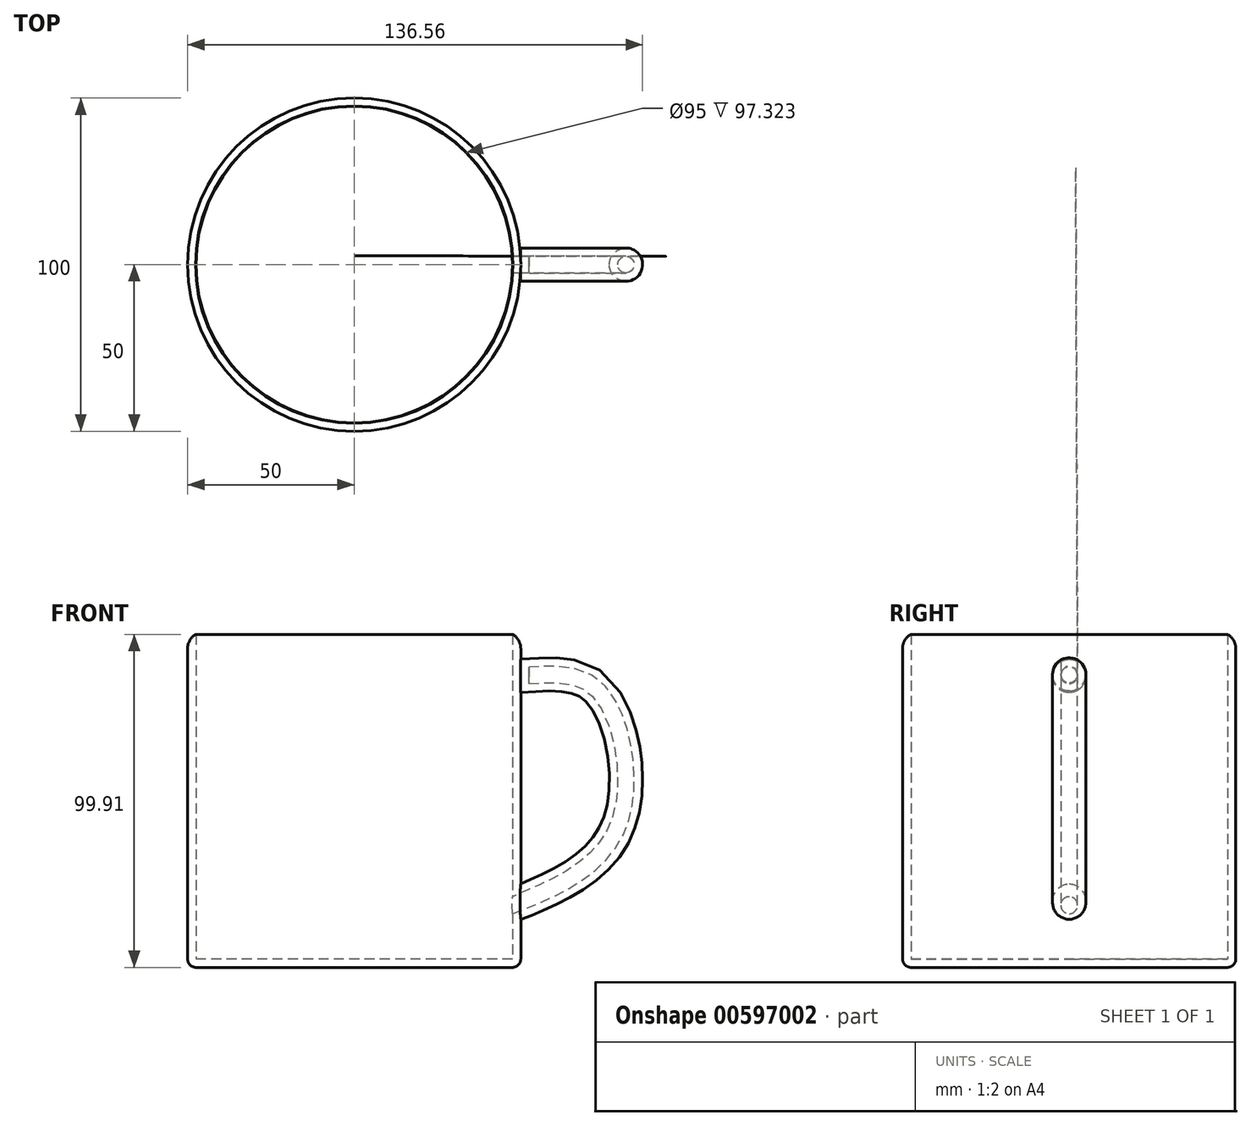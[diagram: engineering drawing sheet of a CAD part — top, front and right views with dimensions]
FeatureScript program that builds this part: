
annotation { "Feature Type Name" : "Feature", "Feature Type Description" : "" }
export const myFeature = defineFeature(function(context is Context, id is Id, definition is map)
    precondition{}
    {
        {
            var Q0;
            Q0=qCreatedBy(makeId("Top.planeOp"),FACE);
            var sketch = newSketch(context, id + "F0", { "sketchPlane" : qUnion([Q0])});
            skCircle(sketch, "E0", {"center": v(0, 0) * mm, "radius": 50 * mm});
            skSolve(sketch);
        }
        {
            var Q0;
            Q0=makeQuery(id+"F0.imprint","IMPRINT",FACE,{"disambiguationData":[TD([[makeQuery(id+"F0.imprint","IMPRINT",EDGE,{"derivedFrom":sQuery(id+"F0.wireOp",EDGE,"E0")}),1.0]])]});
            extrude(context, id + "F1", {"entities" : qUnion([Q0]), "depth" : 100 * mm, "offsetDistance" : 25 * mm});
        }
        {
            var Q0;
            Q0=qCreatedBy(makeId("Right.planeOp"),FACE);
            cPlane(context, id + "F2", {"entities" : qUnion([Q0]), "cplaneType" : CPlaneType.OFFSET, "offset" : 50 * mm, "width" : 150 * mm, "height" : 150 * mm});
        }
        {
            var Q0;
            Q0=qCreatedBy(id+"F2.planeOp",FACE);
            var sketch = newSketch(context, id + "F3", { "sketchPlane" : qUnion([Q0])});
            skCircle(sketch, "E1", {"center": v(0, 87.48) * mm, "radius": 5 * mm});
            skSolve(sketch);
        }
        {
            var Q0;
            Q0=qCreatedBy(makeId("Front.planeOp"),FACE);
            var sketch = newSketch(context, id + "F4", { "sketchPlane" : qUnion([Q0])});
            skFitSpline(sketch, "E2", {"points": [v(49.94, 90.36) * mm, v(74.45, 85.92) * mm, v(83.91, 48.95) * mm, v(69.6, 26.46) * mm, v(51.44, 17.18) * mm, v(41.3, 18.7) * mm], "startDerivative": vector(124.46, 10.01) * mm, "endDerivative": vector(-152.44, 66.76) * mm});
            skSolve(sketch);
        }
        {
            var Q0;
            Q0=makeQuery(id+"F3.imprint","IMPRINT",FACE,{"disambiguationData":[TD([[makeQuery(id+"F3.imprint","IMPRINT",EDGE,{"derivedFrom":sQuery(id+"F3.wireOp",EDGE,"E1")}),1.0]])]});
            var Q1;
            Q1=sQuery(id+"F4.wireOp",EDGE,"E2");
            sweep(context, id + "F5", {"operationType" : NewBodyOperationType.ADD, "profiles" : qUnion([Q0]), "path" : qUnion([Q1])});
        }
        {
            var Q0;
            Q0=makeQuery(id+"F1.opExtrude","CAP_FACE",FACE,{"disambiguationData":[OSD([sQuery(id+"F0.wireOp",EDGE,"E0")])],"isStart":false});
            shell(context, id + "F6", {"entities" : qUnion([Q0]), "thickness" : 2.5 * mm});
        }
        {
            var Q0;
            Q0=makeQuery(id+"F1.opExtrude","CAP_EDGE",EDGE,{"disambiguationData":[OSD([sQuery(id+"F0.wireOp",EDGE,"E0")])],"isStart":false});
            fillet(context, id + "F7", {"entities" : qUnion([Q0]), "radius" : 5 * mm, "tangentPropagation" : true, "allowEdgeOverflow" : false});
        }
        {
            var Q0;
            {var subQ0=sQuery(id+"F0.wireOp",EDGE,"E0");Q0=makeQuery(id+"F7.opFillet","BLEND_EDGE",EDGE,{"blendedFrom":[makeQuery(id+"F1.opExtrude","CAP_EDGE",EDGE,{"disambiguationData":[OSD([subQ0])],"isStart":false}),makeQuery(id+"F6.opShell","OFFSET_FACE",FACE,{"disambiguationData":[OSD([subQ0]),TDD([makeQuery(id+"F1.opExtrude","SWEPT_FACE",FACE,{"disambiguationData":[OSD([subQ0])]})])]})],"blendedInto":[makeQuery(id+"F6.opShell","OFFSET_FACE",FACE,{"disambiguationData":[OSD([subQ0]),TDD([makeQuery(id+"F1.opExtrude","SWEPT_FACE",FACE,{"disambiguationData":[OSD([subQ0])]})])]})]});}
            chamfer(context, id + "F8", {"entities" : qUnion([Q0]), "width" : 0.1 * mm, "tangentPropagation" : true});
        }
        {
            var Q0;
            Q0=makeQuery(id+"F1.opExtrude","CAP_EDGE",EDGE,{"disambiguationData":[OSD([sQuery(id+"F0.wireOp",EDGE,"E0")])],"isStart":true});
            fillet(context, id + "F9", {"entities" : qUnion([Q0]), "radius" : 2.5 * mm, "tangentPropagation" : true, "allowEdgeOverflow" : false});
        }
    });
